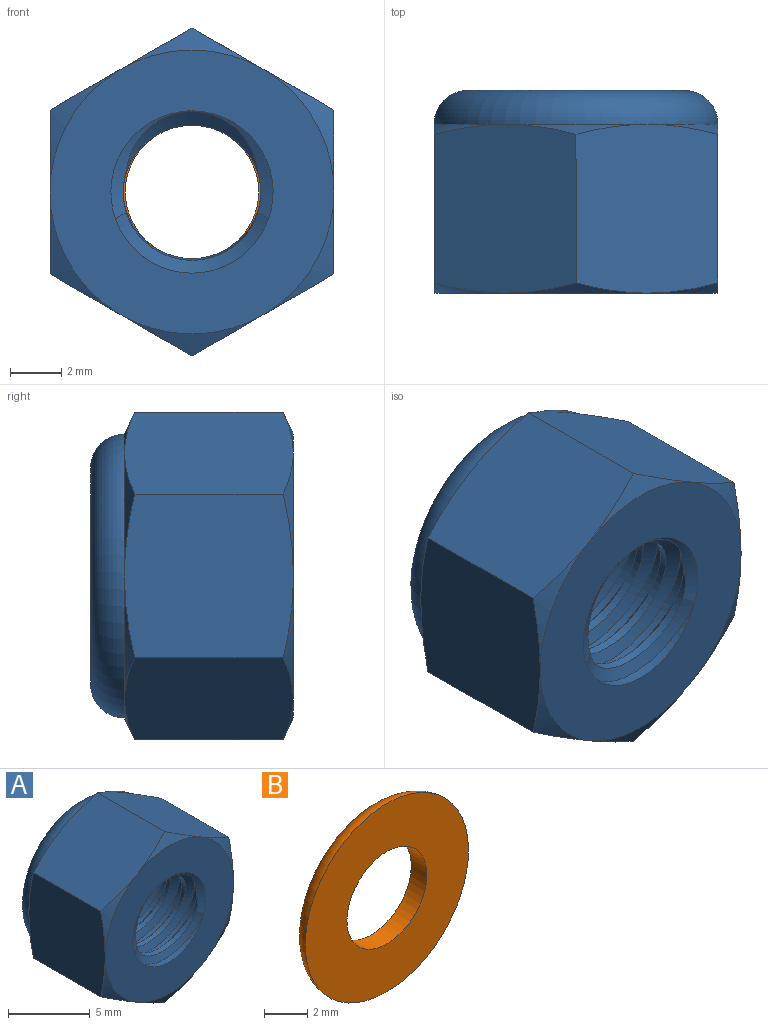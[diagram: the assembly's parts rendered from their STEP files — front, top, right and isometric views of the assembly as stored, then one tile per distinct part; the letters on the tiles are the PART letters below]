
ASSEMBLY  parts=2 mates=1
PART A: 51 faces, bbox 13.3x8.6x13.3 mm
  f0: torus R=4.23mm, axis (0,-1,0), area 57.5mm2, adj f49,f50
  f1: cylinder r=3.42mm len=6.84mm, axis (0,-1,0), area 3.3mm2, adj f27,f50
  f2: torus R=4.23mm, axis (0,-1,0), area 66.3mm2, adj f3,f27,f38,f39,f40,f41,f42
  f3: cone r=5.56mm half-angle=65deg, axis (0,-1,0), area 2.9mm2, adj f2,f47,f48
  f4: cone r=6.42mm half-angle=65deg, axis (0,1,0), area 2.9mm2, adj f28,f44,f45
  f5: cylinder r=3.17mm len=6mm, axis (0,-1,0), area 1.7mm2, adj f25,f28
  f6: cone r=2.69mm half-angle=60deg, axis (0,-0.98,-0.2), area 12mm2, adj f7,f24
  f7: cylinder r=2.69mm len=5.39mm, axis (0,0.98,0.2), area 5.4mm2, adj f6,f8
  f8: cone r=3.38mm half-angle=60deg, axis (0,0.98,0.2), area 12mm2, adj f7,f23
  f9: cone r=2.69mm half-angle=60deg, axis (0,-0.98,-0.2), area 12mm2, adj f10,f23
  f10: cylinder r=2.69mm len=5.39mm, axis (0,0.98,0.2), area 5.4mm2, adj f9,f11
  f11: cone r=3.38mm half-angle=60deg, axis (0,0.98,0.2), area 12mm2, adj f10,f22
  f12: cone r=2.69mm half-angle=60deg, axis (0,-0.98,-0.2), area 12mm2, adj f13,f22
  f13: cylinder r=2.69mm len=5.39mm, axis (0,0.98,0.2), area 5.4mm2, adj f12,f14
  f14: cone r=3.38mm half-angle=60deg, axis (0,0.98,0.2), area 12mm2, adj f13,f21
  f15: cone r=2.69mm half-angle=60deg, axis (0,-0.98,-0.2), area 12mm2, adj f16,f21
  f16: cylinder r=2.69mm len=5.39mm, axis (0,0.98,0.2), area 5.4mm2, adj f15,f17
  f17: cone r=3.38mm half-angle=60deg, axis (0,0.98,0.2), area 12mm2, adj f16,f20
  f18: cylinder r=2.69mm len=5.39mm, axis (0,0.98,0.2), area 2.8mm2, adj f19,f32,f49
  f19: cone r=3.38mm half-angle=60deg, axis (0,0.98,0.2), area 3.5mm2, adj f18,f31,f49
  f20: cylinder r=3.17mm len=6.35mm, axis (0,-1,0), area 6.3mm2, adj f17,f32,f49
  f21: cylinder r=3.17mm len=6.35mm, axis (0,-1,0), area 6.8mm2, adj f14,f15
  f22: cylinder r=3.17mm len=6.35mm, axis (0,-1,0), area 6.8mm2, adj f11,f12
  f23: cylinder r=3.17mm len=6.35mm, axis (0,-1,0), area 6.8mm2, adj f8,f9
  f24: cylinder r=3.17mm len=6.35mm, axis (0,-1,0), area 6.8mm2, adj f6,f26
  f25: cone r=2.69mm half-angle=60deg, axis (0,-0.98,-0.2), area 3.9mm2, adj f5,f29,f30
  f26: cone r=3.38mm half-angle=60deg, axis (0,0.98,0.2), area 8.8mm2, adj f24,f29,f30
  f27: plane 8.47x8.47mm, normal (0,1,0), area 19.5mm2, adj f1,f2
  f28: plane 11.11x11.11mm, normal (0,-1,0), area 65.3mm2, adj f4,f5,f29,f33,f34,f35,f36,f37
  f29: cone r=3.17mm half-angle=65deg, axis (0,-1,0), area 4.1mm2, adj f25,f26,f28,f30
  f30: cylinder r=2.69mm len=5.39mm, axis (0,0.98,0.2), area 2.7mm2, adj f25,f26,f29
  f31: cylinder r=3.17mm len=5.02mm, axis (0,-1,0), area 0.7mm2, adj f19,f49
  f32: cone r=2.69mm half-angle=60deg, axis (0,-0.98,-0.2), area 8.4mm2, adj f18,f20,f49
  f33: cone r=6.42mm half-angle=65deg, axis (0,1,0), area 2.9mm2, adj f28,f47,f48
  f34: cone r=6.42mm half-angle=65deg, axis (0,1,0), area 2.9mm2, adj f28,f43,f48
  f35: cone r=6.42mm half-angle=65deg, axis (0,1,0), area 2.9mm2, adj f28,f43,f44
  f36: cone r=6.42mm half-angle=65deg, axis (0,1,0), area 2.9mm2, adj f28,f45,f46
  f37: cone r=6.42mm half-angle=65deg, axis (0,1,0), area 2.9mm2, adj f28,f46,f47
  f38: cone r=5.56mm half-angle=65deg, axis (0,-1,0), area 2.9mm2, adj f2,f45,f46
  f39: cone r=5.56mm half-angle=65deg, axis (0,-1,0), area 2.9mm2, adj f2,f46,f47
  f40: cone r=5.56mm half-angle=65deg, axis (0,-1,0), area 2.9mm2, adj f2,f44,f45
  f41: cone r=5.56mm half-angle=65deg, axis (0,-1,0), area 2.9mm2, adj f2,f43,f48
  f42: cone r=5.56mm half-angle=65deg, axis (0,-1,0), area 2.9mm2, adj f2,f43,f44
  f43: plane 7.12x6.92mm, normal (1,0,0), area 40.7mm2, adj f34,f35,f41,f42,f44,f48
  f44: plane 7.12x6.06mm, normal (0.5,0,0.87), area 40.7mm2, adj f4,f35,f40,f42,f43,f45
  f45: plane 7.12x6.06mm, normal (-0.5,0,0.87), area 40.7mm2, adj f4,f36,f38,f40,f44,f46
  f46: plane 7.12x6.92mm, normal (-1,0,0), area 40.7mm2, adj f36,f37,f38,f39,f45,f47
  f47: plane 7.12x6.06mm, normal (-0.5,0,-0.87), area 40.7mm2, adj f3,f33,f37,f39,f46,f48
  f48: plane 7.12x6.06mm, normal (0.5,0,-0.87), area 40.7mm2, adj f3,f33,f34,f41,f43,f47
  f49: plane 10.86x10.86mm, normal (0,1,0), area 63.1mm2, adj f0,f18,f19,f20,f31,f32
  f50: plane 8.47x8.47mm, normal (0,-1,0), area 19.5mm2, adj f0,f1
PART B: 4 faces, bbox 11.5x1.1x11.5 mm
  f0: torus R=4.23mm, axis (0,-1,0), area 50.7mm2, adj f2,f3
  f1: cylinder r=2.61mm len=5.22mm, axis (0,-1,0), area 16.7mm2, adj f2,f3
  f2: plane 10.65x10.65mm, normal (0,-1,0), area 67.7mm2, adj f0,f1
  f3: plane 8.47x8.47mm, normal (0,1,0), area 34.9mm2, adj f0,f1
PLACE A t=(-2.94,-4.01,2.49)mm
PLACE B t=(-2.94,-3.93,2.49)mm
MATE fastened B.f1 <-> A.f0  axis (0,-1,0) through (-2.94,3.78,2.49)mm
